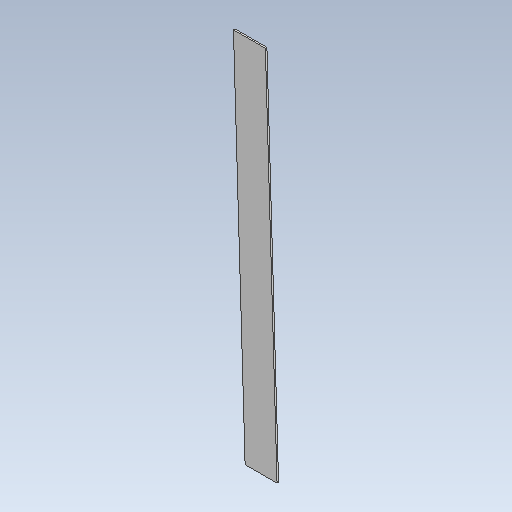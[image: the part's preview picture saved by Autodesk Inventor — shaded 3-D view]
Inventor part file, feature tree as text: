
AUTODESK INVENTOR PART (.ipt)
format: ipt  version: 2020.3 (Build 243373010, 373A)  size: 166,912 bytes
history: native  units: mm
features: other x32, plane x1, extrude x1, sketch x1
ambient origin geometry x8: Origin, YZ Plane, XZ Plane, XY Plane, X Axis, Y Axis, Z Axis, Center Point
bodies: Solid1 (feature_tree)
feature tree (35):
  other  "base_sketch.ipt"
  plane  "Work Plane1"
  extrude  "Extrusion1"  Depth=1.2mm
  other  "stringer"
  other  "stringer_inside"
  other  "bulkhead_main"
  other  "bulkhead_F1"
  other  "bulkhead_front"
  other  "bulkhead_F2"
  other  "bulkhead_B1"
  other  "bulkhead_B2"
  other  "transom"
  other  "stinger_bottom_liner"
  other  "bulkhead_front_tunnel_top"
  other  "bulkhead_front_tunnel_bottom"
  other  "bulkhead_main_top"
  other  "bulkhead_main_tunnel_bottom"
  other  "bulkhead_main_tunnel_standoff"
  other  "bulkhead_front_top"
  other  "bulkhead_front_bottom"
  other  "bulkhead_F1_tunnel_bottom"
  other  "bulkhead_F1_tunnel_top"
  other  "bulkhead_F1_top"
  other  "bulkhead_F1_tunnel_standoff"
  other  "bulkhead_F1_bottom"
  other  "bulkhead_F2_bottom"
  other  "bulkhead_F2_top"
  other  "bulkhead_B1_bottom"
  other  "bulkhead_B1_top"
  other  "bulkhead_B1_tunnel_standoff"
  other  "bulkhead_B1_tunnel_bottom"
  other  "bulkhead_B2_top"
  other  "bulkhead_B2_tunnel_bottom"
  other  "bulkhead_B2_bottom"
  sketch  "Sketch11"  dims[d0=10.0mm d2=35.7mm d3=20.4mm d7=204.0mm d24=45.9mm d27=11.475mm d41=45.9mm d44=0.698132mm d45=122.4mm d48=27.54mm d50=49.7352mm d51=43.146mm d53=62.322mm d54=119.85mm d56=34.5168mm d57=11.5056mm d58=2.48676mm d61=33.558mm d63=0.918mm d66=62.322mm d67=19.176mm d68=19.176mm d70=9.18mm d71=15.0552mm d84=153.0mm d85=41.6925mm d86=102.0mm d87=42.84mm d90=40.8mm d91=24.48mm d95=10.2mm d97=10.340551mm d98=15.510827mm d100=8.541983mm d101=2.55mm d103=112.2mm d104=6.40305mm d105=6.885mm d106=17.2125mm d108=12.202833mm d110=3.582087mm d111=-102.0mm d112=-204.0mm d114=6.981317mm d115=6.981317mm d116=6.981317mm d119=11.760494mm d121=3.635062mm d123=0.729849mm d124=0.364924mm d126=2.390472mm d127=1.195236mm d131=48.8988mm d137=1.86507mm d30=306.0mm d49=45.9mm d55=57.528mm d64=19.176mm d65=18.36mm d96=34.468504mm d99=12.202833mm d107=12.202833mm d109=3.582087mm d120=21.382716mm d122=1.094773mm d125=3.585707mm d128=6.375647mm d130=57.528mm d136=2.48676mm d1=2.0mm d4=1.2mm d5=1.2mm d6=0.0mm]
